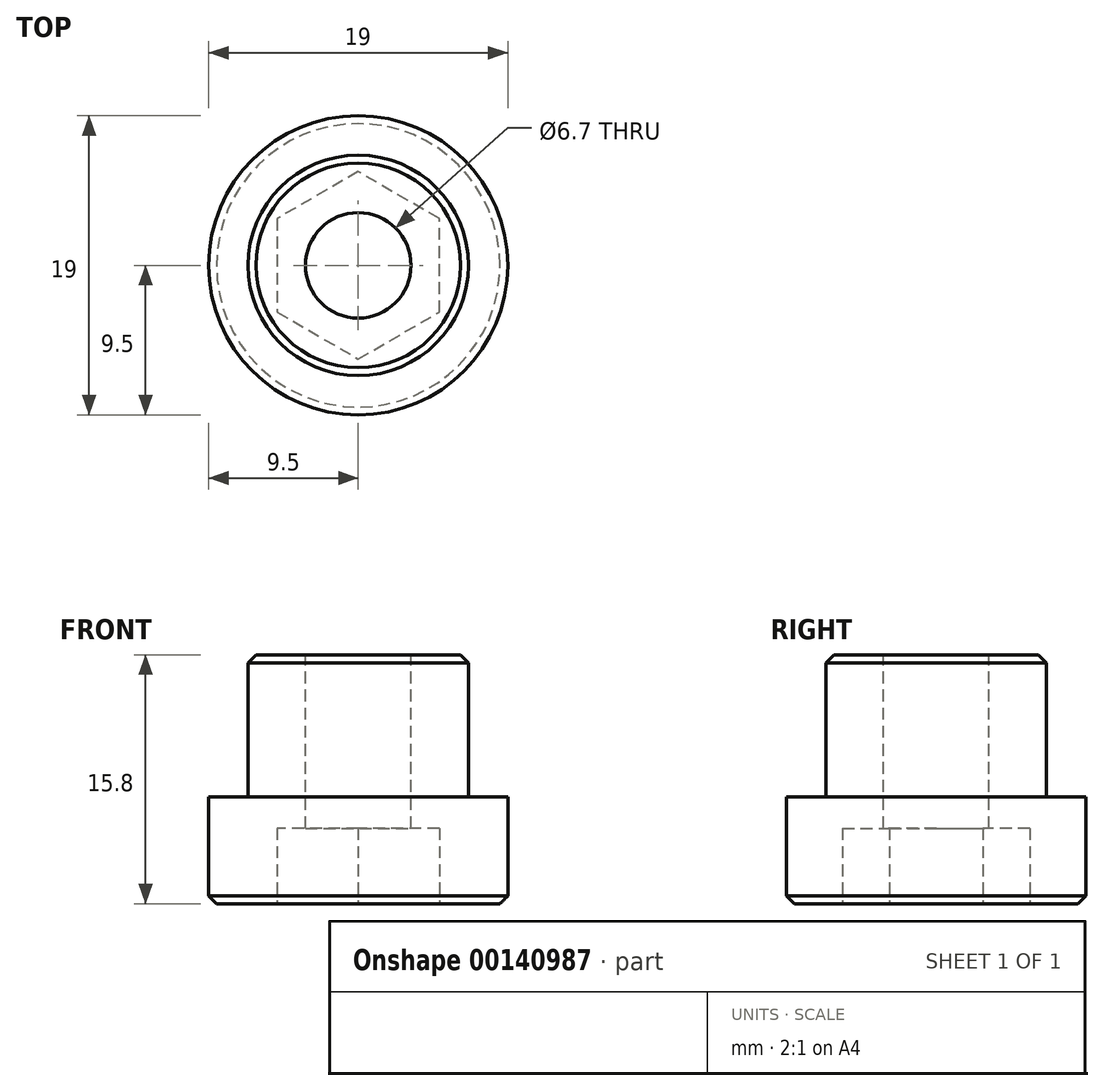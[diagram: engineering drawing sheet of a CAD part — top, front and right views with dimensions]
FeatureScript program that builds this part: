
annotation { "Feature Type Name" : "Feature", "Feature Type Description" : "" }
export const myFeature = defineFeature(function(context is Context, id is Id, definition is map)
    precondition{}
    {
        {
            var Q0;
            Q0=qCreatedBy(makeId("Top.planeOp"),FACE);
            var sketch = newSketch(context, id + "F0", { "sketchPlane" : qUnion([Q0])});
            skCircle(sketch, "E0", {"center": v(0, 0) * mm, "radius": 9.5 * mm});
            skSolve(sketch);
        }
        {
            var Q0;
            Q0 = qSketchRegion(id + "F0", true);
            extrude(context, id + "F1", {"entities" : qUnion([Q0]), "depth" : 6.8 * mm});
        }
        {
            var Q0;
            Q0=makeQuery(id+"F1.opExtrude","CAP_FACE",FACE,{"disambiguationData":[OSD([sQuery(id+"F0.wireOp",EDGE,"E0")])],"isStart":false});
            var sketch = newSketch(context, id + "F2", { "sketchPlane" : qUnion([Q0])});
            skCircle(sketch, "E1", {"center": v(0, 0) * mm, "radius": 7 * mm});
            skSolve(sketch);
        }
        {
            var Q0;
            Q0 = qSketchRegion(id + "F2", true);
            extrude(context, id + "F3", {"entities" : qUnion([Q0]), "operationType" : NewBodyOperationType.ADD, "depth" : 9 * mm});
        }
        {
            var Q0;
            Q0=makeQuery(id+"F1.opExtrude","CAP_FACE",FACE,{"disambiguationData":[OSD([sQuery(id+"F0.wireOp",EDGE,"E0")])],"isStart":true});
            var sketch = newSketch(context, id + "F4", { "sketchPlane" : qUnion([Q0])});
            skCircle(sketch, "E2.cCircle", {"center": v(0, 0) * mm, "radius": 5.15 * mm, "construction": true});
            skLineSegment(sketch, "E2.0", {"start": v(0, -5.95) * mm, "end": v(-5.15, -2.97) * mm});
            skLineSegment(sketch, "E2.1", {"start": v(-5.15, -2.97) * mm, "end": v(-5.15, 2.97) * mm});
            skLineSegment(sketch, "E2.2", {"start": v(-5.15, 2.97) * mm, "end": v(0, 5.95) * mm});
            skLineSegment(sketch, "E2.3", {"start": v(0, 5.95) * mm, "end": v(5.15, 2.97) * mm});
            skLineSegment(sketch, "E2.4", {"start": v(5.15, 2.97) * mm, "end": v(5.15, -2.97) * mm});
            skLineSegment(sketch, "E2.5", {"start": v(5.15, -2.97) * mm, "end": v(0, -5.95) * mm});
            skPoint(sketch, "E2.0.midPoint", {"position": v(-2.58, -4.46) * mm});
            skSolve(sketch);
        }
        {
            var Q0;
            Q0 = qSketchRegion(id + "F4", true);
            extrude(context, id + "F5", {"entities" : qUnion([Q0]), "operationType" : NewBodyOperationType.REMOVE, "oppositeDirection" : true, "depth" : 4.8 * mm});
        }
        {
            var Q0;
            Q0=makeQuery(id+"F3.opExtrude","CAP_FACE",FACE,{"disambiguationData":[OSD([sQuery(id+"F2.wireOp",EDGE,"E1")])],"isStart":false});
            var sketch = newSketch(context, id + "F6", { "sketchPlane" : qUnion([Q0])});
            skCircle(sketch, "E3", {"center": v(0, 0) * mm, "radius": 3.35 * mm});
            skSolve(sketch);
        }
        {
            var Q0;
            Q0 = qSketchRegion(id + "F6", true);
            extrude(context, id + "F7", {"entities" : qUnion([Q0]), "operationType" : NewBodyOperationType.REMOVE, "endBound" : BoundingType.THROUGH_ALL, "oppositeDirection" : true, "depth" : 25 * mm});
        }
        {
            var Q0;
            Q0=makeQuery(id+"F3.opExtrude","CAP_EDGE",EDGE,{"disambiguationData":[OSD([sQuery(id+"F2.wireOp",EDGE,"E1")])],"isStart":false});
            var Q1;
            Q1=makeQuery(id+"F7.boolean.opBoolean","COPY",EDGE,{"derivedFrom":makeQuery(id+"F7.opExtrude","CAP_EDGE",EDGE,{"disambiguationData":[OSD([sQuery(id+"F6.wireOp",EDGE,"E3")])],"isStart":true})});
            var Q2;
            Q2=makeQuery(id+"F1.opExtrude","CAP_EDGE",EDGE,{"disambiguationData":[OSD([sQuery(id+"F0.wireOp",EDGE,"E0")])],"isStart":true});
            chamfer(context, id + "F8", {"entities" : qUnion([Q0, Q1, Q2]), "width" : 0.5 * mm, "tangentPropagation" : true});
        }
    });
